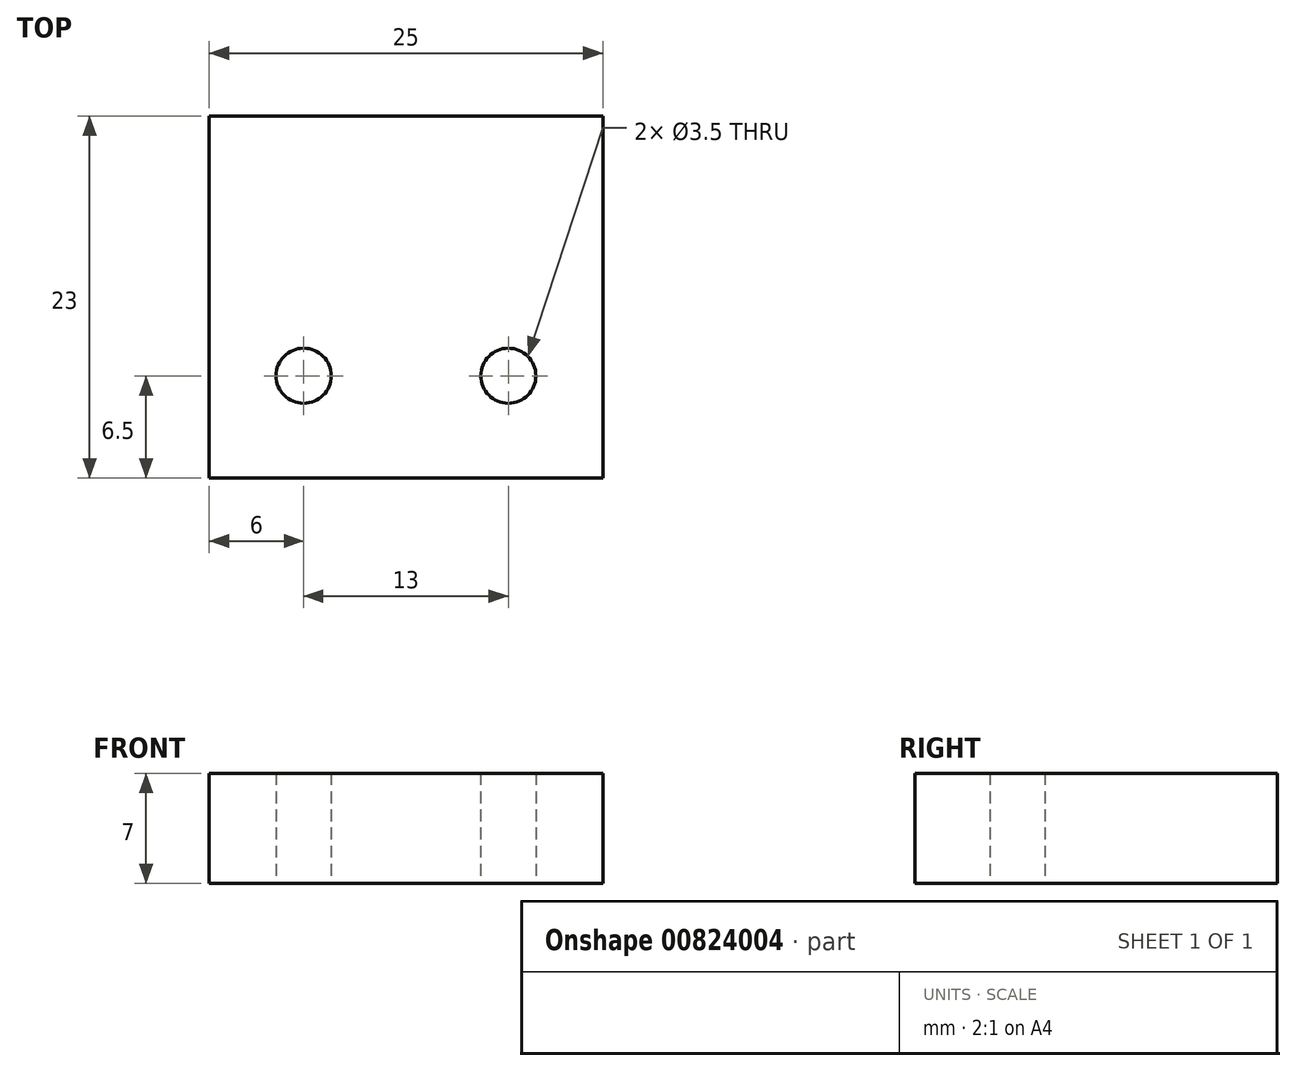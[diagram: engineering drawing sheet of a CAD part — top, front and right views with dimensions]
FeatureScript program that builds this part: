
annotation { "Feature Type Name" : "Feature", "Feature Type Description" : "" }
export const myFeature = defineFeature(function(context is Context, id is Id, definition is map)
    precondition{}
    {
        {
            var Q0;
            Q0=qCreatedBy(makeId("Top.planeOp"),FACE);
            var sketch = newSketch(context, id + "F0", { "sketchPlane" : qUnion([Q0])});
            skLineSegment(sketch, "E0.bottom", {"start": v(0, 0) * mm, "end": v(25, 0) * mm});
            skLineSegment(sketch, "E0.left", {"start": v(0, 0) * mm, "end": v(0, 13) * mm});
            skLineSegment(sketch, "E0.right", {"start": v(25, 0) * mm, "end": v(25, 13) * mm});
            skCircle(sketch, "E1", {"center": v(6, 6.5) * mm, "radius": 1.75 * mm});
            skCircle(sketch, "E2", {"center": v(19, 6.5) * mm, "radius": 1.75 * mm});
            skLineSegment(sketch, "E3", {"start": v(0, 13) * mm, "end": v(0, 23) * mm});
            skLineSegment(sketch, "E4", {"start": v(0, 23) * mm, "end": v(25, 23) * mm});
            skLineSegment(sketch, "E5", {"start": v(25, 23) * mm, "end": v(25, 13) * mm});
            skSolve(sketch);
        }
        {
            var Q0;
            Q0 = qSketchRegion(id + "F0", true);
            extrude(context, id + "F1", {"entities" : qUnion([Q0]), "depth" : 7 * mm, "offsetDistance" : 25 * mm});
        }
    });
